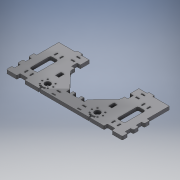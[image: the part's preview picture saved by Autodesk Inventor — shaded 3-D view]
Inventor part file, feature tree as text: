
AUTODESK INVENTOR PART (.ipt)
format: ipt  version: 2016 (Build 200138000, 138)  size: 477,184 bytes
history: native  units: mm
features: extrude x8, sketch x6, fillet x1
ambient origin geometry x8: Origin, YZ Plane, XZ Plane, XY Plane, X Axis, Y Axis, Z Axis, Center Point
bodies: Solid1 (feature_tree)
feature tree (15):
  extrude  "Extrusion1"  Depth=10.0mm
  extrude  "Extrusion2"  Depth=90.0mm
  sketch  "Sketch3"  dims[d6=5.0mm d7=90.0mm]
  extrude  "Extrusion16"  Depth=10.0mm
  extrude  "Extrusion31"  Depth=10.0mm
  extrude  "Extrusion32"  Depth=10.0mm
  extrude  "Extrusion33"  Depth=90.0mm
  extrude  "Extrusion34"  Depth=15.0mm
  extrude  "Extrusion35"  Depth=34.0mm
  fillet  "Fillet10"  Radius=2.0mm
  sketch  "Sketch2"  dims[d4=105.0mm d5=10.0mm]
  sketch  "Sketch8"  dims[d8=10.0mm d9=10.0mm]
  sketch  "Sketch20"  dims[d10=10.0mm d11=10.0mm]
  sketch  "Sketch21"  dims[d12=30.0mm d13=10.0mm]
  sketch  "Sketch22"  dims[d14=3.0mm d15=90.0mm d18=15.0mm d19=34.0mm d20=2.0mm d21=6.0mm d22=0.0mm d23=10.0mm d25=75.0mm d26=45.0mm d27=20.0mm d28=45.0deg d29=2.5mm d30=2.5mm d31=6.0mm d32=0.0mm d41=6.0mm d43=18.0mm d77=68.0mm d102=5.0mm d104=5.0mm d105=10.0mm d129=15.0mm d130=8.0mm d131=2.0mm d132=2.0mm d160=6.0mm d161=6.0mm d162=6.0mm d163=70.0mm d175=10.0mm d177=6.0mm d178=10.0mm d179=16.0mm d180=10.0mm d181=6.0mm d182=55.0mm d183=6.0mm d184=10.0mm d185=10.0mm d186=0.0mm d191=23.0mm d219=12.0mm d238=8.37758mm d239=9.773844mm d286=10.0mm d287=0.0mm d288=4.886922mm d289=2.3mm d290=1.15mm d291=10.0mm d292=0.0mm d293=2.0mm d294=2.0mm d295=7.0mm d296=6.0mm d297=3.0mm d298=20.0mm d299=10.0mm d300=0.0mm d301=5.0mm d302=5.0mm d303=3.0mm d304=10.0mm d305=0.0mm d306=6.0mm d307=10.0mm d308=0.0mm d309=1.5mm d310=14.0mm d314=5.0mm d316=8.0mm d317=10.5mm]
